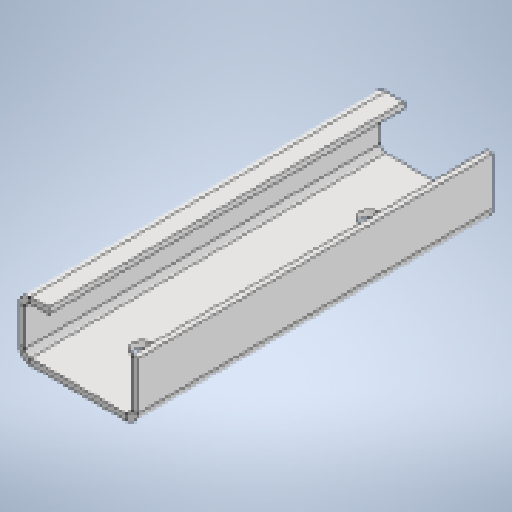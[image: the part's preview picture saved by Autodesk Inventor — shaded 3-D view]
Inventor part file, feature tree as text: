
AUTODESK INVENTOR PART (.ipt)
format: ipt  version: 2025.3 (Build 293356030, 356C)  size: 278,528 bytes
history: native  units: mm
features: other x3, sketch x2, sheet_metal_op x1
ambient origin geometry x8: Origin, YZ Plane, XZ Plane, XY Plane, X Axis, Y Axis, Z Axis, Center Point
bodies: Body1 (feature_tree)
feature tree (6):
  sheet_metal_op  "Face3"
  sketch  "Sketch1"  dims[d61=500.0mm]
  other  "Plate5"
  sketch  "Sketch7"  dims[d154=80.0mm d155=180.0mm d156=3.0mm d157=115.0mm d158=10.0mm d159=3.0mm d160=0.0mm]
  other  "Cut1"
  other  "Definition1"
